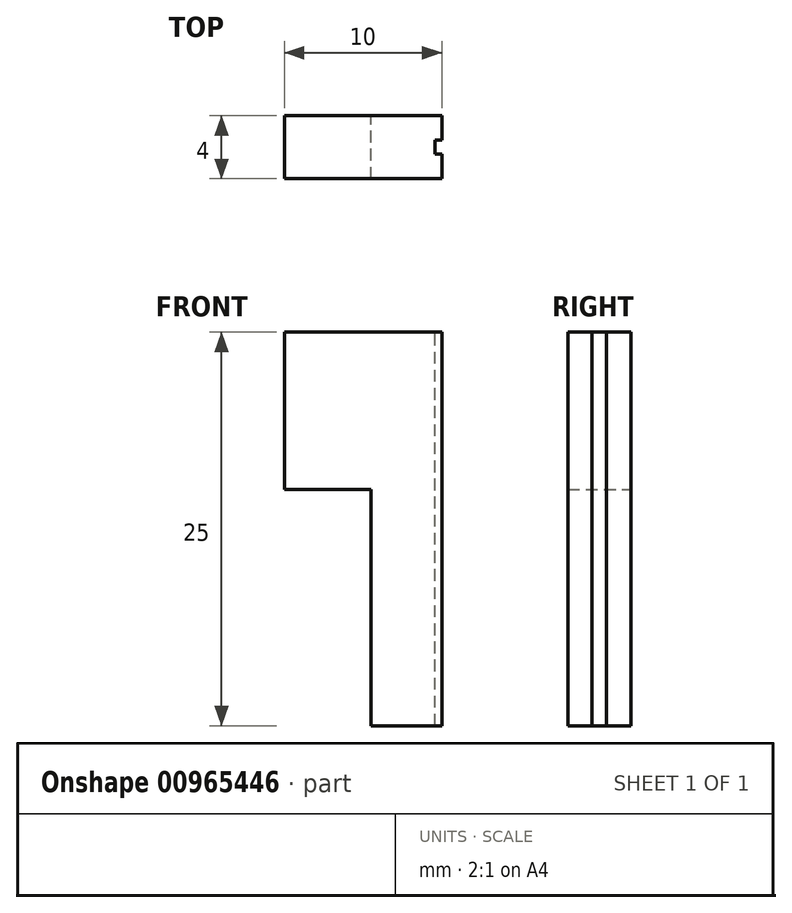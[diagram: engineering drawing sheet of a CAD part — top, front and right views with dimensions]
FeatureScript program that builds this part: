
annotation { "Feature Type Name" : "Feature", "Feature Type Description" : "" }
export const myFeature = defineFeature(function(context is Context, id is Id, definition is map)
    precondition{}
    {
        {
            var Q0;
            Q0=qCreatedBy(makeId("Front.planeOp"),FACE);
            var sketch = newSketch(context, id + "F0", { "sketchPlane" : qUnion([Q0])});
            skLineSegment(sketch, "E0.bottom", {"start": v(10.93, 5.85) * mm, "end": v(2.93, 5.85) * mm});
            skLineSegment(sketch, "E0.top", {"start": v(10.93, -4.15) * mm, "end": v(5.43, -4.15) * mm});
            skLineSegment(sketch, "E0.left", {"start": v(10.93, 5.85) * mm, "end": v(10.93, -4.15) * mm});
            skLineSegment(sketch, "E0.right", {"start": v(-9.07, 5.85) * mm, "end": v(-9.07, -4.15) * mm});
            skPoint(sketch, "E0.middle", {"position": v(0.93, 0.85) * mm});
            skPoint(sketch, "E1.middle", {"position": v(0.93, 5.85) * mm});
            skLineSegment(sketch, "E2.top", {"start": v(5.43, -19.15) * mm, "end": v(-3.57, -19.15) * mm});
            skLineSegment(sketch, "E2.left", {"start": v(5.43, -4.15) * mm, "end": v(5.43, -19.15) * mm});
            skLineSegment(sketch, "E2.right", {"start": v(-3.57, -4.15) * mm, "end": v(-3.57, -19.15) * mm});
            skPoint(sketch, "E2.middle", {"position": v(0.93, -11.65) * mm});
            skPoint(sketch, "E2.middle.positionSnap0", {"position": v(0.93, -4.15) * mm});
            skPoint(sketch, "E2.centerSnap0", {"position": v(0.93, -4.15) * mm});
            skPoint(sketch, "E3.orphan", {"position": v(2.93, -24.15) * mm});
            skPoint(sketch, "E4.orphan", {"position": v(-1.07, -24.15) * mm});
            skLineSegment(sketch, "E5.trimOffspring", {"start": v(-3.57, -4.15) * mm, "end": v(-9.07, -4.15) * mm});
            skLineSegment(sketch, "E6.trimOffspring", {"start": v(-1.07, 5.85) * mm, "end": v(-9.07, 5.85) * mm});
            skLineSegment(sketch, "E7", {"start": v(-1.07, 5.85) * mm, "end": v(2.93, 5.85) * mm});
            skSolve(sketch);
        }
        {
            var Q0;
            Q0=qSketchRegion(id+"F0",true);
            extrude(context, id + "F1", {"entities" : qUnion([Q0]), "depth" : 4 * mm, "offsetDistance" : 25 * mm});
        }
        {
            var Q0;
            Q0=makeQuery(id+"F1.opExtrude","SWEPT_FACE",FACE,{"disambiguationData":[OSD([sQuery(id+"F0.wireOp",EDGE,"E0.bottom"),sQuery(id+"F0.wireOp",EDGE,"E6.trimOffspring"),sQuery(id+"F0.wireOp",EDGE,"E7")])]});
            var sketch = newSketch(context, id + "F2", { "sketchPlane" : qUnion([Q0])});
            skLineSegment(sketch, "E8.bottom", {"start": v(10.93, 0) * mm, "end": v(0.93, 0) * mm});
            skLineSegment(sketch, "E8.top", {"start": v(10.93, -4) * mm, "end": v(0.93, -4) * mm});
            skLineSegment(sketch, "E8.left", {"start": v(10.93, 0) * mm, "end": v(10.93, -4) * mm});
            skLineSegment(sketch, "E8.right", {"start": v(0.93, 0) * mm, "end": v(0.93, -1.55) * mm});
            skPoint(sketch, "E8.middle", {"position": v(5.93, -2) * mm});
            skPoint(sketch, "E8.middle.positionSnap0", {"position": v(10.93, -2) * mm});
            skPoint(sketch, "E8.centerSnap0", {"position": v(10.93, -2) * mm});
            skLineSegment(sketch, "E9.bottom", {"start": v(0.48, -2.45) * mm, "end": v(0.93, -2.45) * mm});
            skLineSegment(sketch, "E9.top", {"start": v(0.48, -1.55) * mm, "end": v(0.93, -1.55) * mm});
            skLineSegment(sketch, "E9.left", {"start": v(0.48, -2.45) * mm, "end": v(0.48, -1.55) * mm});
            skPoint(sketch, "E9.middle", {"position": v(0.93, -2) * mm});
            skLineSegment(sketch, "E10.trimOffspring", {"start": v(0.93, -2.45) * mm, "end": v(0.93, -4) * mm});
            skPoint(sketch, "E9.right.end.orphan", {"position": v(1.38, -1.55) * mm});
            skPoint(sketch, "E11.orphan", {"position": v(1.38, -2.45) * mm});
            skSolve(sketch);
        }
        {
            var Q0;
            Q0=qSketchRegion(id+"F2",true);
            extrude(context, id + "F3", {"entities" : qUnion([Q0]), "operationType" : NewBodyOperationType.REMOVE, "oppositeDirection" : true, "depth" : 25 * mm, "offsetDistance" : 25 * mm});
        }
    });
